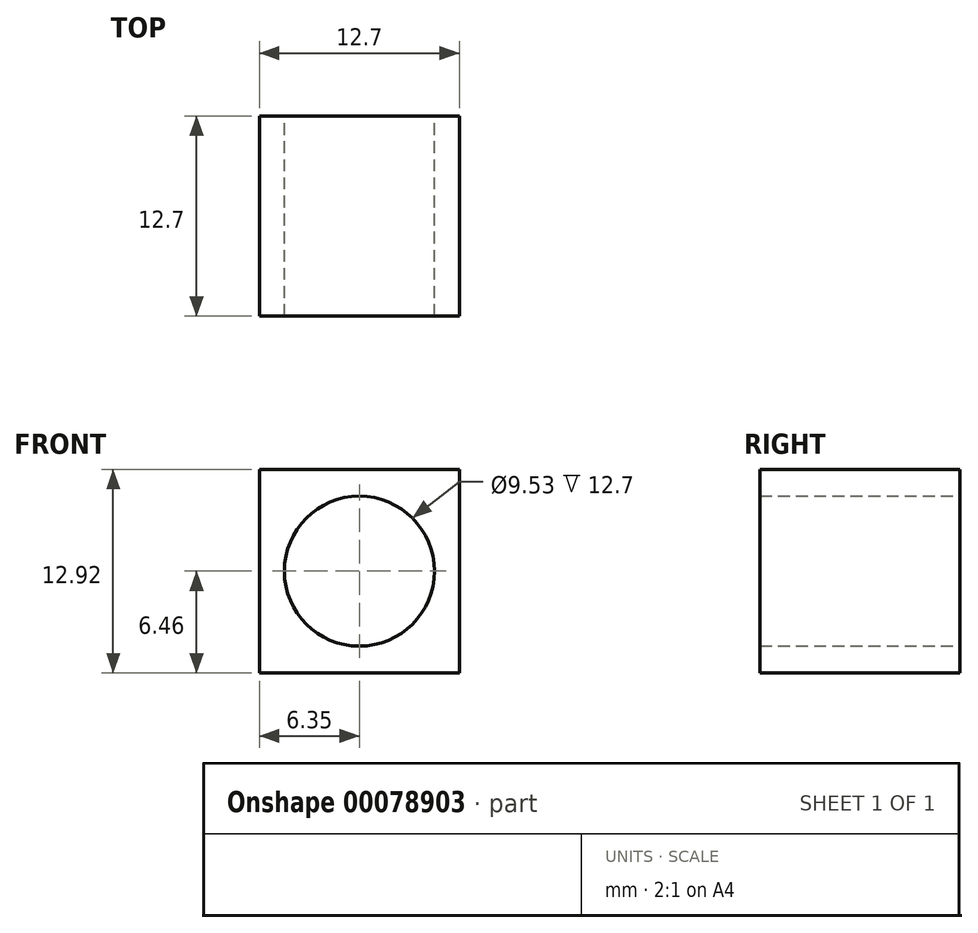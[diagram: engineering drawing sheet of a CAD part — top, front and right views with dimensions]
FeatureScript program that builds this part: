
annotation { "Feature Type Name" : "Feature", "Feature Type Description" : "" }
export const myFeature = defineFeature(function(context is Context, id is Id, definition is map)
    precondition{}
    {
        {
            var Q0;
            Q0=qCreatedBy(makeId("Front.planeOp"),FACE);
            var sketch = newSketch(context, id + "F0", { "sketchPlane" : qUnion([Q0])});
            skLineSegment(sketch, "E0.bottom", {"start": v(6.35, 6.46) * mm, "end": v(-6.35, 6.46) * mm});
            skLineSegment(sketch, "E0.top", {"start": v(6.35, -6.46) * mm, "end": v(-6.35, -6.46) * mm});
            skLineSegment(sketch, "E0.left", {"start": v(6.35, 6.46) * mm, "end": v(6.35, -6.46) * mm});
            skLineSegment(sketch, "E0.right", {"start": v(-6.35, 6.46) * mm, "end": v(-6.35, -6.46) * mm});
            skPoint(sketch, "E0.middle", {"position": v(0, 0) * mm});
            skCircle(sketch, "E1", {"center": v(0, 0) * mm, "radius": 4.76 * mm});
            skSolve(sketch);
        }
        {
            var Q0;
            Q0=makeQuery(id+"F0.imprint","IMPRINT",FACE,{"disambiguationData":[TD([[makeQuery(id+"F0.imprint","IMPRINT",EDGE,{"derivedFrom":sQuery(id+"F0.wireOp",EDGE,"E0.bottom")}),1.0]])]});
            extrude(context, id + "F1", {"entities" : qUnion([Q0]), "depth" : 12.7 * mm});
        }
    });
